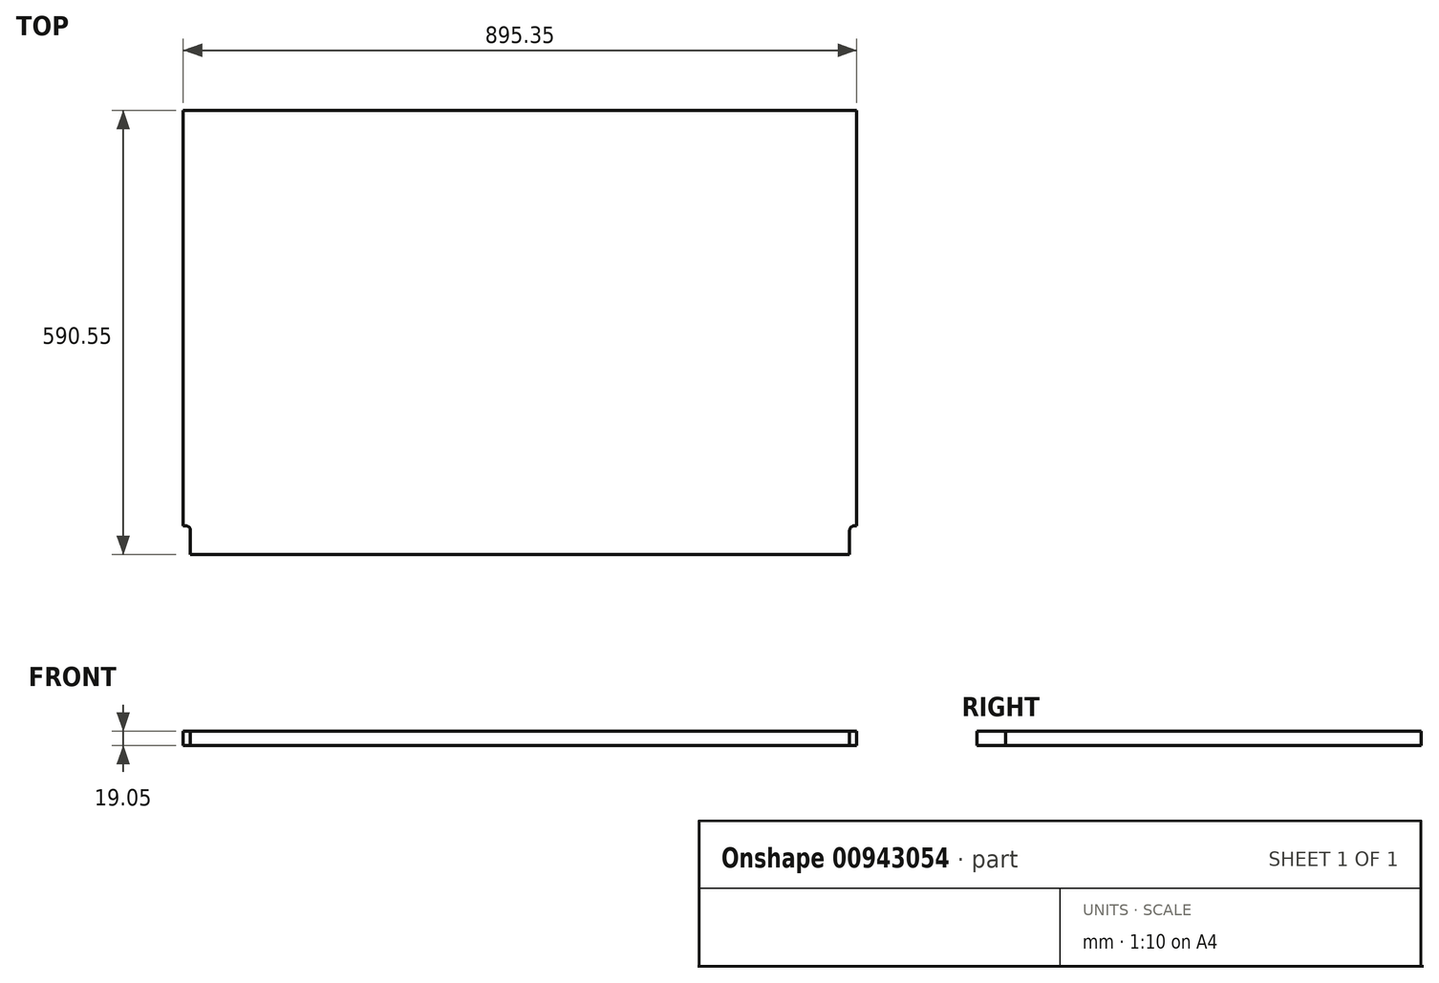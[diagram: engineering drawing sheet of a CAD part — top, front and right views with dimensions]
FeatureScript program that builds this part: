
annotation { "Feature Type Name" : "Feature", "Feature Type Description" : "" }
export const myFeature = defineFeature(function(context is Context, id is Id, definition is map)
    precondition{}
    {
        {
            var Q0;
            Q0=qCreatedBy(makeId("Top.planeOp"),FACE);
            var sketch = newSketch(context, id + "F0", { "sketchPlane" : qUnion([Q0])});
            skLineSegment(sketch, "E0.bottom", {"start": v(0, 0) * mm, "end": v(895.35, 0) * mm});
            skLineSegment(sketch, "E0.top", {"start": v(0, -590.55) * mm, "end": v(895.35, -590.55) * mm});
            skLineSegment(sketch, "E0.left", {"start": v(0, 0) * mm, "end": v(0, -590.55) * mm});
            skLineSegment(sketch, "E0.right", {"start": v(895.35, 0) * mm, "end": v(895.35, -590.55) * mm});
            skLineSegment(sketch, "E1", {"start": v(9.53, -590.55) * mm, "end": v(9.53, -558.8) * mm});
            skLineSegment(sketch, "E2", {"start": v(0, -552.45) * mm, "end": v(3.18, -552.45) * mm});
            skArc(sketch, "E3", {"start": v(9.53, -558.8) * mm, "mid": v(7.67, -554.3) * mm, "end": v(3.18, -552.45) * mm});
            skLineSegment(sketch, "E4", {"start": v(447.68, 0) * mm, "end": v(447.68, -590.55) * mm, "construction": true});
            skLineSegment(sketch, "E5.MirrorCS", {"start": v(895.35, -552.45) * mm, "end": v(892.18, -552.45) * mm});
            skArc(sketch, "E6.MirrorCS", {"start": v(885.83, -558.8) * mm, "mid": v(887.68, -554.3) * mm, "end": v(892.18, -552.45) * mm});
            skLineSegment(sketch, "E7.MirrorCS", {"start": v(885.83, -590.55) * mm, "end": v(885.83, -558.8) * mm});
            skSolve(sketch);
        }
        {
            var Q0;
            {var subQ1=sQuery(id+"F0.wireOp",EDGE,"E0.bottom");Q0=makeQuery(id+"F0.imprint","IMPRINT",FACE,{"disambiguationData":[TD([[makeQuery(id+"F0.imprint","IMPRINT",EDGE,{"derivedFrom":subQ1}),-1.0]])]});}
            extrude(context, id + "F1", {"entities" : qUnion([Q0]), "depth" : 19.05 * mm, "offsetDistance" : 25.4 * mm});
        }
    });
